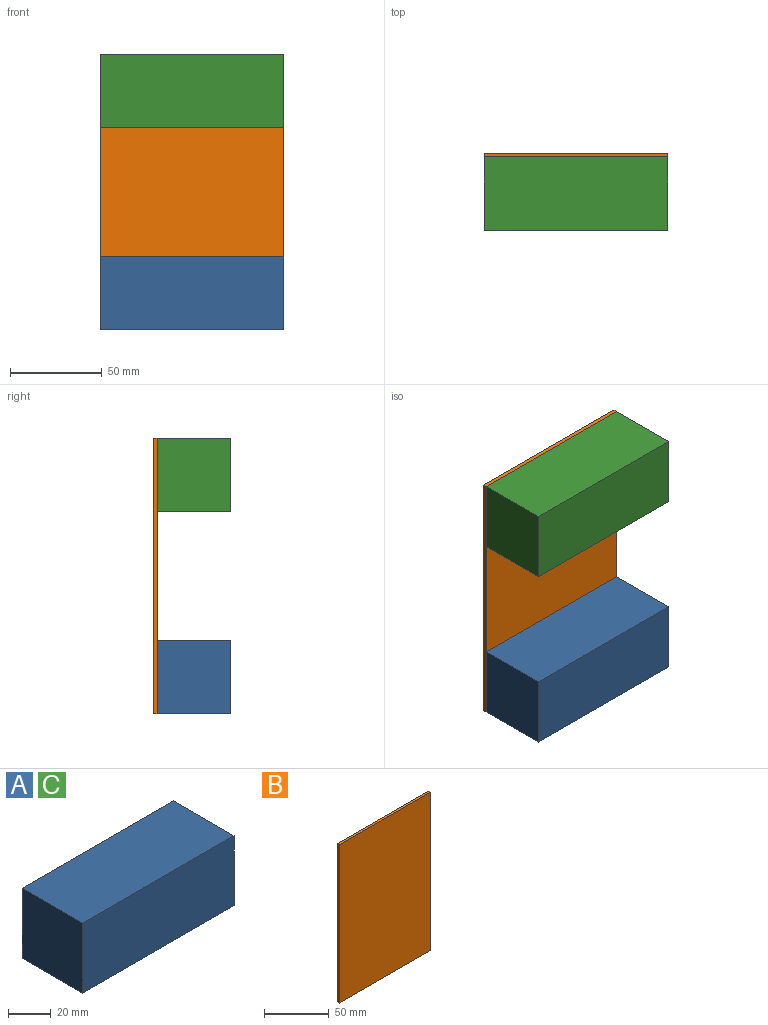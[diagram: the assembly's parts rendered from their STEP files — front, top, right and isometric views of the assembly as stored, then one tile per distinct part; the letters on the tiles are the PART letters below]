
ASSEMBLY  parts=3 mates=1
PART A: 6 faces, bbox 100x40x40 mm
  f0: plane 100x40mm, normal (0,0,1), area 4000mm2, adj f1,f3,f4,f5
  f1: plane 40x40mm, normal (-1,0,0), area 1600mm2, adj f0,f2,f4,f5
  f2: plane 100x40mm, normal (0,0,-1), area 4000mm2, adj f1,f3,f4,f5
  f3: plane 40x40mm, normal (1,0,0), area 1600mm2, adj f0,f2,f4,f5
  f4: plane 100x40mm, normal (0,-1,0), area 4000mm2, adj f0,f1,f2,f3
  f5: plane 100x40mm, normal (0,1,0), area 4000mm2, adj f0,f1,f2,f3
PART B: 6 faces, bbox 100x2x150 mm
  f0: plane 100x2mm, normal (0,0,1), area 200mm2, adj f1,f3,f4,f5
  f1: plane 150x2mm, normal (-1,0,0), area 300mm2, adj f0,f2,f4,f5
  f2: plane 100x2mm, normal (0,0,-1), area 200mm2, adj f1,f3,f4,f5
  f3: plane 150x2mm, normal (1,0,0), area 300mm2, adj f0,f2,f4,f5
  f4: plane 150x100mm, normal (0,-1,0), area 15000mm2, adj f0,f1,f2,f3
  f5: plane 150x100mm, normal (0,1,0), area 15000mm2, adj f0,f1,f2,f3
PART C: same geometry as A
PLACE A t=(-41.36,34.17,-134.47)mm
PLACE B t=(-41.36,36.17,-24.47)mm
PLACE C t=(-41.36,34.17,-24.47)mm
MATE fastened C.f5 <-> B.f4  axis (0,1,0) through (8.64,34.17,-44.47)mm
